# Revit family: FR_PG-1000_vereinfacht
name_source: partatom
category: Allgemeines Modell
revit_build: Autodesk Revit 2018 (Build: 20181015_0930(x64)
units: mm (PartAtom-declared; Revit-internal decimal feet)

## family parameters
Beim Laden mit Abzugskörper schneiden = Ja
Bemaßung runder Anschluss = Durchmesser verwenden
Gemeinsam genutzt = Ja
Kann Basisbauteil für Bewehrung sein = Nein
OmniClass-Nummer = 23.70.50.00
OmniClass-Titel = Liquid Waste Handling Services
Raumberechnungspunkt = Nein
Teiletyp = Normal

## types (1)
- MEADrain PG 1000 vereinfacht
    Bauelement = Caniveau_eaux de surface
    Bauteil, Entwässerung = Caniveau de drainage
    Beschreibung = Canivea monolothique en bétton polymère. Hauteur 50mm
    Classe de charge Caniveau = C 250
    Construction élément de drainage = Caniveau avec profilé de peigne
    Diamètre exterieur Manchon = 0 mm  [stored 0 ft]
    Documents de mise en œuvre = conformément aux dessins et à la description du produits.
    Fiche technique produit = https://www.mea-group.com
    Hauteur = 50 mm  [stored 0.164042 ft]
    Hersteller = MEA Bautechnik GmbH business uniteMEA Water Management
    IfcDescription = Canivea monolothique en bétton polymère. Hauteur 50mm
    IfcExportAs = IfcWasteTerminalType
    IfcExportType = USERDEFINED
    Largeur = 100 mm  [stored 0.328084 ft]
    Largeur du Caniveau mm = 150
    Largeur utile = 100 mm  [stored 0.328084 ft]
    MEA Planungshilfe = https://www.mea-group.com
    Materiaux = Polymerbeton
    Materiaux,enrobage Béton/ fondation = PCC-Mörtel/Epoxy-Mörtel
    Poids = 7.24KGM
    Référence (Art.Nr) = 010155602
    STLB-Bau Mustervorlage = https://www.stlb-bau-online.de
    Technique de montage = Caniveau seuls
    Typ élément de drainage = Typ M
    URL = https://www.mea-group.com
    guid = cf6c1bd8-9bf4-4563-8c57-07955e2378ac

note: [stored X ft] marks values corroborated as IEEE doubles in the binary element streams (Revit-internal decimal feet)

## geometry (parser evidence)
native form markers: Extrusion x12
no freeform markers — native parametric forms only
